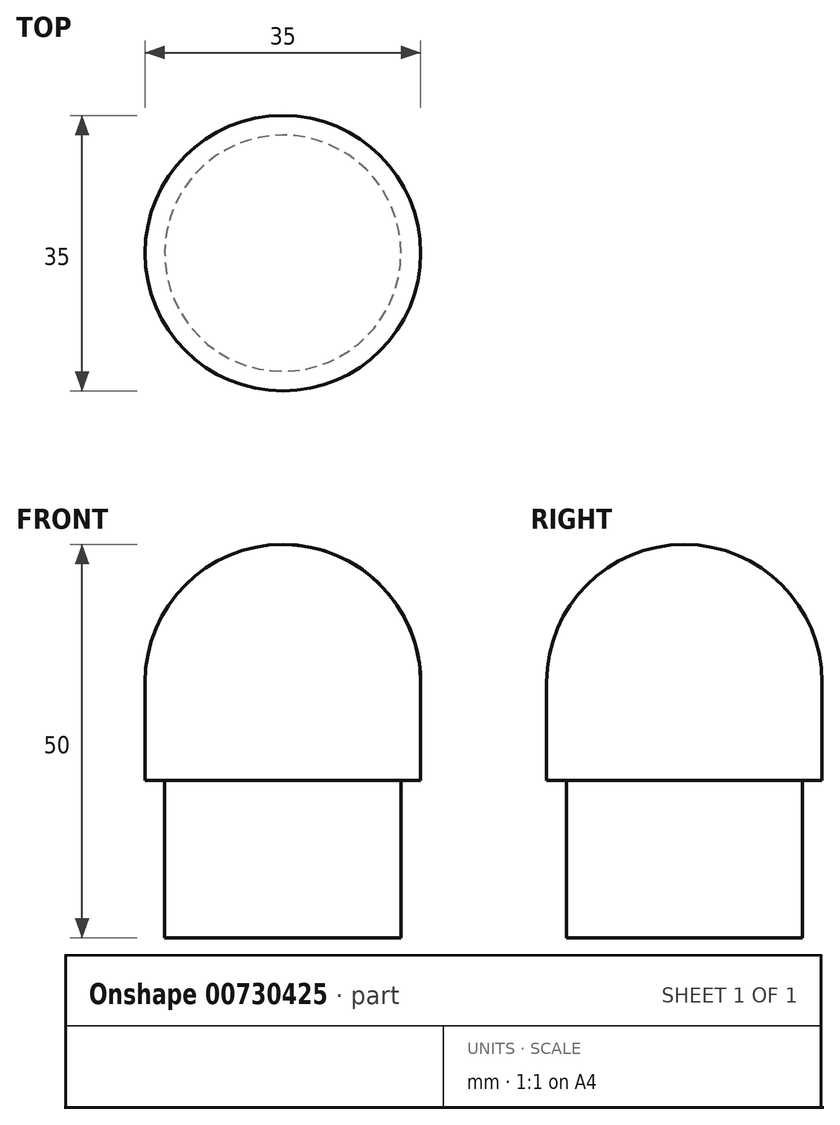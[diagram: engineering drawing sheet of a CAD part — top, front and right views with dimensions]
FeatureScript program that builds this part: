
annotation { "Feature Type Name" : "Feature", "Feature Type Description" : "" }
export const myFeature = defineFeature(function(context is Context, id is Id, definition is map)
    precondition{}
    {
        {
            var Q0;
            Q0=qCreatedBy(makeId("Front.planeOp"),FACE);
            var sketch = newSketch(context, id + "F0", { "sketchPlane" : qUnion([Q0])});
            skLineSegment(sketch, "E0", {"start": v(0, -49.71) * mm, "end": v(15, -49.71) * mm});
            skLineSegment(sketch, "E1", {"start": v(15, -49.71) * mm, "end": v(15, -29.71) * mm});
            skLineSegment(sketch, "E2", {"start": v(15, -29.71) * mm, "end": v(17.5, -29.71) * mm});
            skLineSegment(sketch, "E3", {"start": v(17.5, -29.71) * mm, "end": v(17.5, -17.21) * mm});
            skArc(sketch, "E4", {"start": v(17.5, -17.21) * mm, "mid": v(12.37, -4.84) * mm, "end": v(0, 0.29) * mm});
            skLineSegment(sketch, "E5", {"start": v(0, -49.71) * mm, "end": v(0, 0.29) * mm});
            skSolve(sketch);
        }
        {
            var Q0;
            Q0=makeQuery(id+"F0.imprint","IMPRINT",FACE,{"disambiguationData":[TD([[makeQuery(id+"F0.imprint","IMPRINT",EDGE,{"derivedFrom":sQuery(id+"F0.wireOp",EDGE,"E0")}),1.0]])]});
            var Q1;
            Q1=sQuery(id+"F0.wireOp",EDGE,"E5");
            revolve(context, id + "F1", {"surfaceOperationType" : NewSurfaceOperationType.NEW, "entities" : qUnion([Q0]), "axis" : qUnion([Q1]), "revolveType" : RevolveType.FULL});
        }
    });
